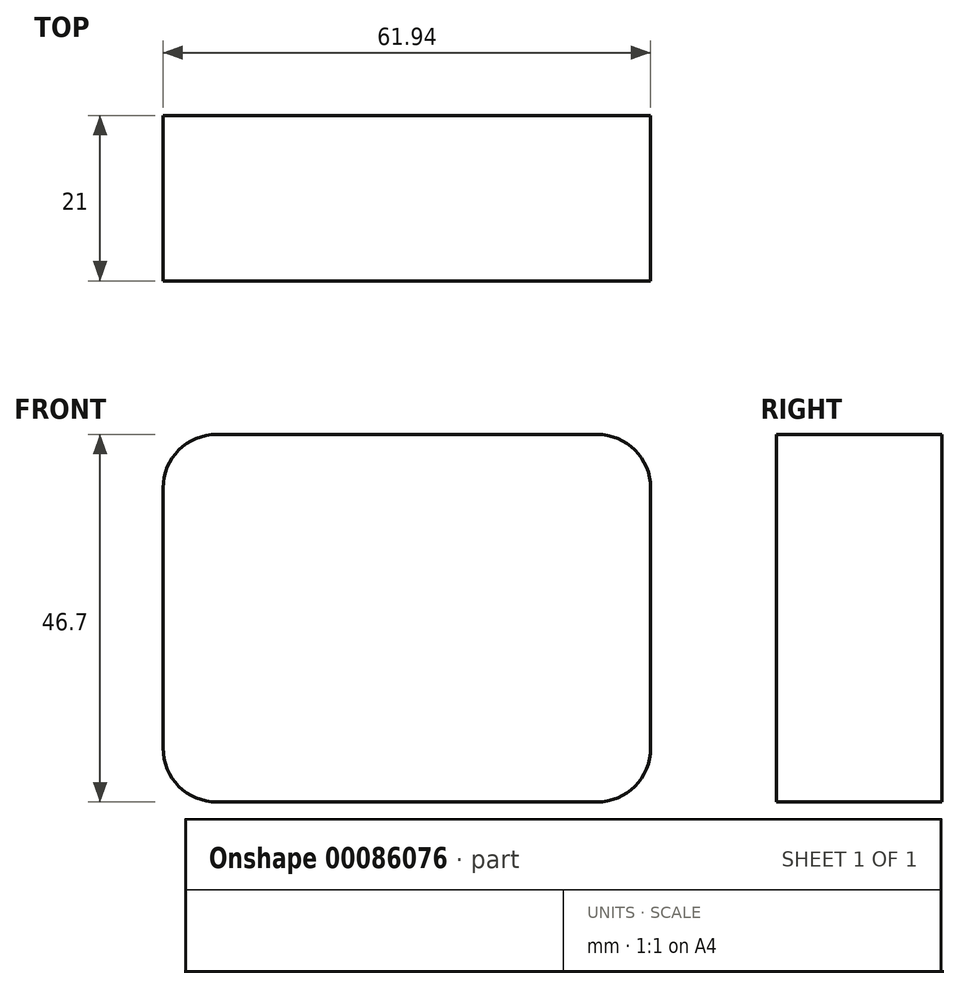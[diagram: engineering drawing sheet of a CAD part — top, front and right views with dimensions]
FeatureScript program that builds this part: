
annotation { "Feature Type Name" : "Feature", "Feature Type Description" : "" }
export const myFeature = defineFeature(function(context is Context, id is Id, definition is map)
    precondition{}
    {
        {
            var Q0;
            Q0=qCreatedBy(makeId("Front.planeOp"),FACE);
            var sketch = newSketch(context, id + "F0", { "sketchPlane" : qUnion([Q0])});
            skLineSegment(sketch, "E0.bottom", {"start": v(24.13, -19.05) * mm, "end": v(-24.13, -19.05) * mm});
            skLineSegment(sketch, "E0.top", {"start": v(24.13, 19.05) * mm, "end": v(-24.13, 19.05) * mm});
            skLineSegment(sketch, "E0.left", {"start": v(26.67, -16.51) * mm, "end": v(26.67, 16.51) * mm});
            skLineSegment(sketch, "E0.right", {"start": v(-26.67, -16.51) * mm, "end": v(-26.67, 16.5) * mm});
            skPoint(sketch, "E0.middle", {"position": v(0, 0) * mm});
            skPoint(sketch, "E1.visualSharp", {"position": v(-26.67, 19.05) * mm});
            skArc(sketch, "E1.filletArc", {"start": v(-24.13, 19.05) * mm, "mid": v(-25.93, 18.3) * mm, "end": v(-26.67, 16.5) * mm});
            skPoint(sketch, "E2.visualSharp", {"position": v(26.67, 19.05) * mm});
            skArc(sketch, "E2.filletArc", {"start": v(26.67, 16.51) * mm, "mid": v(25.93, 18.3) * mm, "end": v(24.13, 19.05) * mm});
            skPoint(sketch, "E3.visualSharp", {"position": v(26.67, -19.05) * mm});
            skArc(sketch, "E3.filletArc", {"start": v(24.13, -19.05) * mm, "mid": v(25.93, -18.3) * mm, "end": v(26.67, -16.51) * mm});
            skPoint(sketch, "E4.visualSharp", {"position": v(-26.67, -19.05) * mm});
            skArc(sketch, "E4.filletArc", {"start": v(-26.67, -16.51) * mm, "mid": v(-25.93, -18.3) * mm, "end": v(-24.13, -19.05) * mm});
            skLineSegment(sketch, "E5.bottom", {"start": v(13.5, -10.95) * mm, "end": v(-13.5, -10.95) * mm});
            skLineSegment(sketch, "E5.top", {"start": v(13.5, 16.05) * mm, "end": v(-13.5, 16.05) * mm});
            skLineSegment(sketch, "E5.left", {"start": v(13.5, -10.95) * mm, "end": v(13.5, 16.05) * mm});
            skLineSegment(sketch, "E5.right", {"start": v(-13.5, -10.95) * mm, "end": v(-13.5, 16.05) * mm});
            skPoint(sketch, "E5.middle", {"position": v(0, 2.55) * mm});
            skLineSegment(sketch, "E6.bottom", {"start": v(12.5, -3.05) * mm, "end": v(-12.5, -3.05) * mm});
            skLineSegment(sketch, "E6.top", {"start": v(12.5, 10.95) * mm, "end": v(-12.5, 10.95) * mm});
            skLineSegment(sketch, "E6.left", {"start": v(12.5, -3.05) * mm, "end": v(12.5, 10.95) * mm});
            skLineSegment(sketch, "E6.right", {"start": v(-12.5, -3.05) * mm, "end": v(-12.5, 10.95) * mm});
            skPoint(sketch, "E6.middle", {"position": v(0, 3.95) * mm});
            skLineSegment(sketch, "E7.bottom", {"start": v(22.67, -13.55) * mm, "end": v(16.67, -13.55) * mm});
            skLineSegment(sketch, "E7.top", {"start": v(22.67, -7.55) * mm, "end": v(16.67, -7.55) * mm});
            skLineSegment(sketch, "E7.left", {"start": v(22.67, -13.55) * mm, "end": v(22.67, -7.55) * mm});
            skLineSegment(sketch, "E7.right", {"start": v(16.67, -13.55) * mm, "end": v(16.67, -7.55) * mm});
            skPoint(sketch, "E7.middle", {"position": v(19.67, -10.55) * mm});
            skCircle(sketch, "E8", {"center": v(19.67, -10.55) * mm, "radius": 1.5 * mm});
            skLineSegment(sketch, "E9.MirrorCS", {"start": v(-22.67, -7.55) * mm, "end": v(-16.67, -7.55) * mm});
            skLineSegment(sketch, "E10.MirrorCS", {"start": v(-16.67, -13.55) * mm, "end": v(-16.67, -7.55) * mm});
            skPoint(sketch, "E11.MirrorP", {"position": v(-19.67, -10.55) * mm});
            skCircle(sketch, "E12.MirrorC", {"center": v(-19.67, -10.55) * mm, "radius": 1.5 * mm});
            skLineSegment(sketch, "E13.MirrorCS", {"start": v(-22.67, -13.55) * mm, "end": v(-16.67, -13.55) * mm});
            skLineSegment(sketch, "E14.MirrorCS", {"start": v(-22.67, -13.55) * mm, "end": v(-22.67, -7.55) * mm});
            skArc(sketch, "E15.0", {"start": v(29.17, 16.51) * mm, "mid": v(27.7, 20.07) * mm, "end": v(24.13, 21.55) * mm});
            skLineSegment(sketch, "E15.1", {"start": v(29.17, -16.51) * mm, "end": v(29.17, 16.51) * mm});
            skLineSegment(sketch, "E15.2", {"start": v(24.13, 21.55) * mm, "end": v(-24.13, 21.55) * mm});
            skArc(sketch, "E15.3", {"start": v(24.13, -21.55) * mm, "mid": v(27.7, -20.07) * mm, "end": v(29.17, -16.51) * mm});
            skArc(sketch, "E15.4", {"start": v(-24.13, 21.55) * mm, "mid": v(-27.7, 20.07) * mm, "end": v(-29.17, 16.5) * mm});
            skLineSegment(sketch, "E15.5", {"start": v(-29.17, -16.51) * mm, "end": v(-29.17, 16.5) * mm});
            skArc(sketch, "E15.6", {"start": v(-29.17, -16.51) * mm, "mid": v(-27.7, -20.07) * mm, "end": v(-24.13, -21.55) * mm});
            skLineSegment(sketch, "E15.7", {"start": v(24.13, -21.55) * mm, "end": v(-24.13, -21.55) * mm});
            skArc(sketch, "E16.0", {"start": v(30.97, 16.51) * mm, "mid": v(28.97, 21.35) * mm, "end": v(24.13, 23.35) * mm});
            skLineSegment(sketch, "E16.1", {"start": v(30.97, -16.51) * mm, "end": v(30.97, 16.51) * mm});
            skLineSegment(sketch, "E16.2", {"start": v(24.13, 23.35) * mm, "end": v(-24.13, 23.35) * mm});
            skArc(sketch, "E16.3", {"start": v(24.13, -23.35) * mm, "mid": v(28.97, -21.35) * mm, "end": v(30.97, -16.51) * mm});
            skArc(sketch, "E16.4", {"start": v(-24.13, 23.35) * mm, "mid": v(-28.97, 21.35) * mm, "end": v(-30.97, 16.5) * mm});
            skLineSegment(sketch, "E16.5", {"start": v(-30.97, -16.51) * mm, "end": v(-30.97, 16.5) * mm});
            skArc(sketch, "E16.6", {"start": v(-30.97, -16.51) * mm, "mid": v(-28.97, -21.35) * mm, "end": v(-24.13, -23.35) * mm});
            skLineSegment(sketch, "E16.7", {"start": v(24.13, -23.35) * mm, "end": v(-24.13, -23.35) * mm});
            skCircle(sketch, "E17.0", {"center": v(19.67, -10.55) * mm, "radius": 2 * mm});
            skCircle(sketch, "E18.MirrorC", {"center": v(-19.67, -10.55) * mm, "radius": 2 * mm});
            skSolve(sketch);
        }
        {
            var Q0;
            Q0=makeQuery(id+"F0.imprint","IMPRINT",FACE,{"disambiguationData":[TD([[makeQuery(id+"F0.imprint","IMPRINT",EDGE,{"derivedFrom":sQuery(id+"F0.wireOp",EDGE,"E0.bottom")}),1.0]])]});
            var Q1;
            Q1=makeQuery(id+"F0.imprint","IMPRINT",FACE,{"disambiguationData":[TD([[makeQuery(id+"F0.imprint","IMPRINT",EDGE,{"derivedFrom":sQuery(id+"F0.wireOp",EDGE,"E5.bottom")}),-1.0]])]});
            var Q2;
            Q2=makeQuery(id+"F0.imprint","IMPRINT",FACE,{"disambiguationData":[TD([[makeQuery(id+"F0.imprint","IMPRINT",EDGE,{"derivedFrom":sQuery(id+"F0.wireOp",EDGE,"E7.bottom")}),-1.0]])]});
            var Q3;
            Q3=makeQuery(id+"F0.imprint","IMPRINT",FACE,{"disambiguationData":[TD([[makeQuery(id+"F0.imprint","IMPRINT",EDGE,{"derivedFrom":sQuery(id+"F0.wireOp",EDGE,"E9.MirrorCS")}),-1.0]])]});
            var Q4;
            Q4=makeQuery(id+"F0.imprint","IMPRINT",FACE,{"disambiguationData":[TD([[makeQuery(id+"F0.imprint","IMPRINT",EDGE,{"derivedFrom":sQuery(id+"F0.wireOp",EDGE,"E0.bottom")}),-1.0]])]});
            var Q5;
            Q5=makeQuery(id+"F0.imprint","IMPRINT",FACE,{"disambiguationData":[TD([[makeQuery(id+"F0.imprint","IMPRINT",EDGE,{"derivedFrom":sQuery(id+"F0.wireOp",EDGE,"E6.bottom")}),-1.0]])]});
            var Q6;
            Q6=makeQuery(id+"F0.imprint","IMPRINT",FACE,{"disambiguationData":[TD([[makeQuery(id+"F0.imprint","IMPRINT",EDGE,{"derivedFrom":sQuery(id+"F0.wireOp",EDGE,"E8")}),-1.0]])]});
            var Q7;
            Q7=makeQuery(id+"F0.imprint","IMPRINT",FACE,{"disambiguationData":[TD([[makeQuery(id+"F0.imprint","IMPRINT",EDGE,{"derivedFrom":sQuery(id+"F0.wireOp",EDGE,"E12.MirrorC")}),1.0]])]});
            var Q8;
            Q8=makeQuery(id+"F0.imprint","IMPRINT",FACE,{"disambiguationData":[TD([[makeQuery(id+"F0.imprint","IMPRINT",EDGE,{"derivedFrom":sQuery(id+"F0.wireOp",EDGE,"E12.MirrorC")}),-1.0]])]});
            var Q9;
            Q9=makeQuery(id+"F0.imprint","IMPRINT",FACE,{"disambiguationData":[TD([[makeQuery(id+"F0.imprint","IMPRINT",EDGE,{"derivedFrom":sQuery(id+"F0.wireOp",EDGE,"E8")}),1.0]])]});
            var Q10;
            Q10=makeQuery(id+"F0.imprint","IMPRINT",FACE,{"disambiguationData":[TD([[makeQuery(id+"F0.imprint","IMPRINT",EDGE,{"derivedFrom":sQuery(id+"F0.wireOp",EDGE,"E15.0")}),-1.0]])]});
            extrude(context, id + "F1", {"entities" : qUnion([Q0, Q1, Q2, Q3, Q4, Q5, Q6, Q7, Q8, Q9, Q10]), "endBound" : BoundingType.SYMMETRIC, "depth" : 21 * mm});
        }
    });
